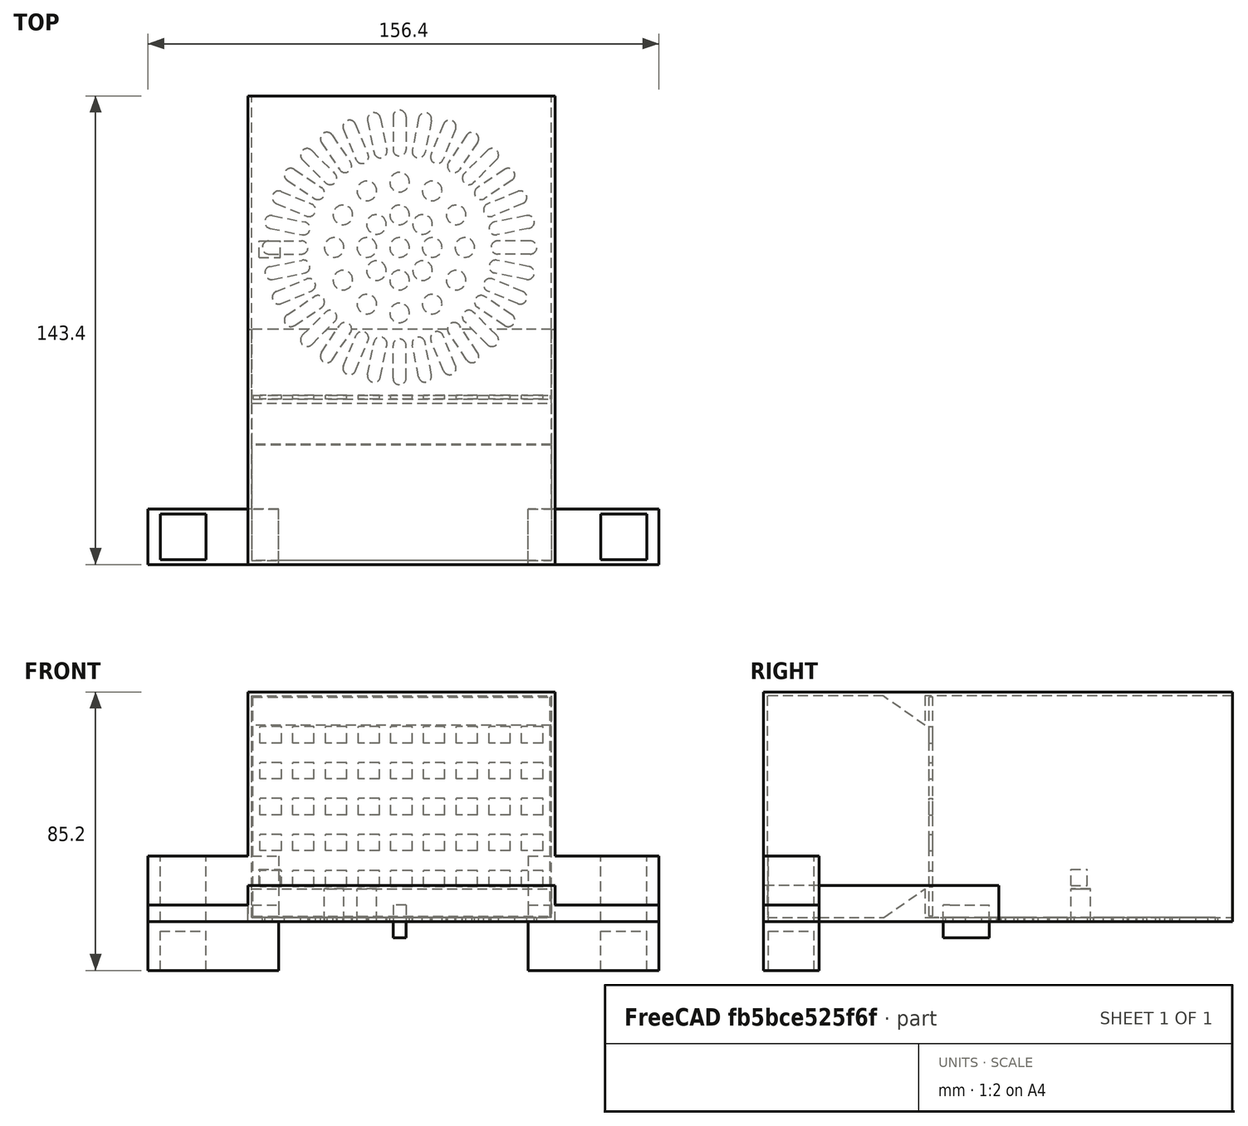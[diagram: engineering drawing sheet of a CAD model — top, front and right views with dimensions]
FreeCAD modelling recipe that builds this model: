
FCSTD DOCUMENT  (FreeCAD 0.19R24276 (Git))
Label: venti_to_aac
License: All rights reserved
LicenseURL: http://en.wikipedia.org/wiki/All_rights_reserved
objects: Part::Box×14, Part::Cut×11, Part::MultiFuse×7, Part::Cylinder×6, Part::FeaturePython×4, PartDesign::ShapeBinder×3, Sketcher::SketchObject×3, PartDesign::Pad×3, PartDesign::Body×3, Mesh::Feature×3, Part::Feature×1
note: 54 computed .brp shape members not serialized (recipe doc carries the construction recipe); baked Part::Feature solids carry a one-line shape summary decoded from their .brp

FEATURE [Part::Cylinder] Cylinder
  Angle = 360
  AttacherType = Attacher::AttachEngine3D
  Height = 1.2
  Radius = 45
FEATURE [Part::Cylinder] Cylinder002
  Angle = 360
  AttacherType = Attacher::AttachEngine3D
  Height = 10
  Radius = 3
FEATURE [Part::Cut] Cut
  Base = -> Cylinder
  Tool = -> Cylinder002
FEATURE [PartDesign::ShapeBinder] CopyCut
  TraceSupport = false
FEATURE [Sketcher::SketchObject] Sketch
  FullyConstrained = true
  MapMode = 5
  Placement = pos=(0,0,0) rot=(1,0,0;3.14159rad)
  Support = -> [CopyCut]
  sketch-geometry (4):
    g0: ArcOfCircle CenterX=-40 CenterY=0 CenterZ=0 NormalX=0 NormalY=0 NormalZ=1 AngleXU=0 Radius=2 StartAngle=1.5708 EndAngle=4.71239
    g1: ArcOfCircle CenterX=-30 CenterY=0 CenterZ=0 NormalX=0 NormalY=0 NormalZ=1 AngleXU=0 Radius=2 StartAngle=4.71239 EndAngle=7.85398
    g2: LineSegment StartX=-40 StartY=-2 StartZ=0 EndX=-30 EndY=-2 EndZ=0
    g3: LineSegment StartX=-40 StartY=2 StartZ=0 EndX=-30 EndY=2 EndZ=0
  constraints (10):
    c: Tangent(g0,g3) = 1.5708
    c: Tangent(g0,g2) = -1.5708
    c: Tangent(g2,g1) = -1.5708
    c: Tangent(g3,g1) = 1.5708
    c: Horizontal(g2)
    c: Equal(g0,g1)
    c: PointOnObject(g0,g-1)
    c: DistanceY(g0,g0) = 4
    c: DistanceX(g0,g1) = 10
    c: DistanceX(g0,g-1) = 40
FEATURE [PartDesign::Pad] Pad
  Direction = (1,1,1)
  Length = 10
  Length2 = 100
  Midplane = true
  Profile = -> Sketch
  Type = 0
FEATURE [PartDesign::Body] Body
  Group = -> [CopyCut,Sketch,Pad]
  Origin = -> Origin
  Placement = pos=(0,0,0) rot=(0,0,1;1.5708rad)
  Tip = -> Pad
FEATURE [Part::FeaturePython] Array  # Draft array (typed FeaturePython)
  Angle = 360
  ArrayType = 1
  Axis = (0,0,1)
  Base = -> Body
  Center = (0,0,0)
  Count = 32
  ExpandArray = false
  Fuse = false
  IntervalAxis = (0,0,0)
  IntervalX = (50,0,0)
  IntervalY = (0,50,0)
  IntervalZ = (0,0,50)
  NumberCircles = 3
  NumberPolar = 32
  NumberX = 2
  NumberY = 2
  NumberZ = 1
  PlacementList = 32 placements: [(0,0,0),(0,0,0),(0,0,0),(0,0,0),(0,0,0),(0,0,0),(0,0,0),(0,0,0),(0,0,0),(0,0,0),(0,0,0),(0,0,0),(0,0,0),(0,0,0),(0,0,0),(0,0,0),(0,0,0),(0,0,0),(0,0,0),(0,0,0),(0,0,0),(0,0,0),(0,0,0),(0,0,0),(0,0,0),(0,0,0),(0,0,0),(0,0,0),(0,0,0),(0,0,0),(0,0,0),(0,0,0)]
  RadialDistance = 50
  ScaleList = (32) [(1,1,1),(1,1,1),(1,1,1),(1,1,1),(1,1,1),(1,1,1),(1,1,1),(1,1,1),(1,1,1),(1,1,1),(1,1,1),(1,1,1),(1,1,1),(1,1,1),(1,1,1),(1,1,1),(1,1,1),(1,1,1),+14 more]
  Symmetry = 1
  TangentialDistance = 25
FEATURE [Part::Cut] Cut001
  Base = -> Cut
  Tool = -> Array
FEATURE [Part::Cylinder] Cylinder006
  Angle = 360
  AttacherType = Attacher::AttachEngine3D
  Height = 10
  Radius = 45
FEATURE [Part::Box] Box  label="Cube"
  AttacherType = Attacher::AttachEngine3D
  Height = 1.2
  Length = 92.8
  Placement = pos=(-46.4,-46.4,0) rot=(0,0,1;0rad)
  Width = 92.8
FEATURE [Part::Cut] Cut002
  Base = -> Box
  Tool = -> Cylinder006
FEATURE [Part::MultiFuse] Fusion
  Shapes = -> [Cut001,Cut002]
FEATURE [Part::Box] Box001  label="Cube001"
  AttacherType = Attacher::AttachEngine3D
  Height = 1.2
  Length = 92.8
  Placement = pos=(-46.4,-97,0) rot=(0,0,1;0rad)
  Width = 50.6
FEATURE [Part::MultiFuse] Fusion001
  Shapes = -> [Fusion,Box001]
FEATURE [Part::Box] Box002  label="Cube002"
  AttacherType = Attacher::AttachEngine3D
  Height = 70.2
  Length = 1.2
  Placement = pos=(46.4,-97,0) rot=(0,0,1;0rad)
  Width = 143.4
FEATURE [Part::Box] Box003  label="Cube003"
  AttacherType = Attacher::AttachEngine3D
  Height = 70.2
  Length = 1.2
  Placement = pos=(-46.4,-97,0) rot=(0,0,1;0rad)
  Width = 143.4
FEATURE [Part::Box] Box004  label="Cube004"
  AttacherType = Attacher::AttachEngine3D
  Height = 1.2
  Length = 94
  Placement = pos=(-46.4,-97,69) rot=(0,0,1;0rad)
  Width = 143.4
FEATURE [Part::MultiFuse] Fusion002
  Shapes = -> [Fusion001,Box002,Box003,Box004]
FEATURE [Part::Box] Box005  label="Cube005"
  AttacherType = Attacher::AttachEngine3D
  Height = 70.2
  Length = 94
  Placement = pos=(-46.4,-97,0) rot=(0,0,1;0rad)
  Width = 1.2
FEATURE [PartDesign::ShapeBinder] CopyFusion002001
  TraceSupport = false
FEATURE [Sketcher::SketchObject] Sketch001
  FullyConstrained = true
  MapMode = 5
  Placement = pos=(47.6,0,0) rot=(0.57735,0.57735,0.57735;2.0944rad)
  Support = -> [CopyFusion002001]
  sketch-geometry (3):
    g0: LineSegment StartX=0 StartY=0 StartZ=0 EndX=0 EndY=10 EndZ=0
    g1: LineSegment StartX=0 StartY=10 StartZ=0 EndX=-14.2815 EndY=0 EndZ=0
    g2: LineSegment StartX=-14.2815 StartY=0 StartZ=0 EndX=0 EndY=0 EndZ=0
  constraints (8):
    c: Coincident(g-1,g0)
    c: PointOnObject(g0,g-2)
    c: Coincident(g0,g1)
    c: PointOnObject(g1,g-1)
    c: Coincident(g1,g2)
    c: Coincident(g2,g0)
    c: Angle(g2,g1) = 0.610865
    c: DistanceY(g0,g0) = 10
FEATURE [PartDesign::Pad] Pad001
  Direction = (1,1,1)
  Length = 94
  Length2 = 100
  Profile = -> Sketch001
  Type = 0
FEATURE [PartDesign::Body] Body001
  Group = -> [CopyFusion002001,Sketch001,Pad001]
  Origin = -> Origin001
  Placement = pos=(-94,-47.6,0) rot=(0,0,1;0rad)
  Tip = -> Pad001
FEATURE [PartDesign::ShapeBinder] CopyFusion002002
  TraceSupport = false
FEATURE [Sketcher::SketchObject] Sketch002
  FullyConstrained = true
  MapMode = 5
  Placement = pos=(47.6,0,0) rot=(0.57735,0.57735,0.57735;2.0944rad)
  Support = -> [CopyFusion002002]
  sketch-geometry (3):
    g0: LineSegment StartX=0 StartY=0 StartZ=0 EndX=0 EndY=10 EndZ=0
    g1: LineSegment StartX=0 StartY=10 StartZ=0 EndX=-14.2815 EndY=0 EndZ=0
    g2: LineSegment StartX=-14.2815 StartY=0 StartZ=0 EndX=0 EndY=0 EndZ=0
  constraints (8):
    c: Coincident(g-1,g0)
    c: PointOnObject(g0,g-2)
    c: Coincident(g0,g1)
    c: PointOnObject(g1,g-1)
    c: Coincident(g1,g2)
    c: Coincident(g2,g0)
    c: Angle(g2,g1) = 0.610865
    c: DistanceY(g0,g0) = 10
FEATURE [PartDesign::Pad] Pad002
  Direction = (1,1,1)
  Length = 94
  Length2 = 100
  Profile = -> Sketch002
  Type = 0
FEATURE [PartDesign::Body] Body002
  Group = -> [CopyFusion002002,Sketch002,Pad002]
  Origin = -> Origin002
  Placement = pos=(95.2,-47.6,70) rot=(0,1,0;3.14159rad)
  Tip = -> Pad002
FEATURE [Part::MultiFuse] Fusion003
  Shapes = -> [Fusion002,Box005]
FEATURE [Part::MultiFuse] Fusion004  label="caja_grande"
  Shapes = -> [Fusion003,Body002,Body001]
FEATURE [Part::Box] Box006  label="Cube006"
  AttacherType = Attacher::AttachEngine3D
  Height = 1.2
  Length = 91
  Placement = pos=(-44.9,0,1.6) rot=(1,0,0;1.5708rad)
  Width = 67
FEATURE [Part::Box] Box007  label="Cube007"
  AttacherType = Attacher::AttachEngine3D
  Height = 5
  Length = 6.5
  Placement = pos=(-43,-3,11) rot=(0,0,1;0rad)
  Width = 5
FEATURE [Part::FeaturePython] Array001  # Draft array (typed FeaturePython)
  Angle = 360
  ArrayType = 0
  Axis = (0,0,1)
  Base = -> Box007
  Center = (0,0,0)
  Count = 45
  ExpandArray = false
  Fuse = false
  IntervalAxis = (0,0,0)
  IntervalX = (10,0,0)
  IntervalY = (0,10,0)
  IntervalZ = (0,0,11)
  NumberCircles = 3
  NumberPolar = 5
  NumberX = 9
  NumberY = 1
  NumberZ = 5
  Placement = pos=(0.35,0,-0.4) rot=(0,0,1;0rad)
  PlacementList = 45 placements: [(-43,-3,11),(-43,-3,22),(-43,-3,33),(-43,-3,44),(-43,-3,55),(-33,-3,11),(-33,-3,22),(-33,-3,33),(-33,-3,44),(-33,-3,55),(-23,-3,11),(-23,-3,22),(-23,-3,33),(-23,-3,44),(-23,-3,55),(-13,-3,11),(-13,-3,22),(-13,-3,33),(-13,-3,44),(-13,-3,55),(-3,-3,11),(-3,-3,22),(-3,-3,33),(-3,-3,44),(-3,-3,55),(7,-3,11),(7,-3,22),(7,-3,33),(7,-3,44),(7,-3,55),(17,-3,11),(17,-3,22),(17,-3,33),(17,-3,44),(17,-3,55),+10 more]
  RadialDistance = 50
  ScaleList = (45) [(1,1,1),(1,1,1),(1,1,1),(1,1,1),(1,1,1),(1,1,1),(1,1,1),(1,1,1),(1,1,1),(1,1,1),(1,1,1),(1,1,1),(1,1,1),(1,1,1),(1,1,1),(1,1,1),(1,1,1),(1,1,1),+27 more]
  Symmetry = 1
  TangentialDistance = 25
FEATURE [Part::Cut] Cut003  label="rejilla"
  Base = -> Box006
  Placement = pos=(0,-45.2,0) rot=(0,0,1;0rad)
  Tool = -> Array001
FEATURE [Part::Box] Box008  label="Cube008"
  AttacherType = Attacher::AttachEngine3D
  Height = 20
  Length = 40
  Placement = pos=(-77,-97,-15) rot=(0,0,1;0rad)
  Width = 17
FEATURE [Part::Box] Box009  label="Cube009"
  AttacherType = Attacher::AttachEngine3D
  Height = 20
  Length = 40
  Placement = pos=(39.4,-97,-15) rot=(0,0,1;0rad)
  Width = 17
FEATURE [Part::Box] Box010  label="Cube010"
  AttacherType = Attacher::AttachEngine3D
  Height = 52
  Length = 14
  Placement = pos=(61.6,-95.5,-15) rot=(0,0,1;0rad)
  Width = 14
FEATURE [Part::Box] Box011  label="Cube011"
  AttacherType = Attacher::AttachEngine3D
  Height = 35
  Length = 14
  Placement = pos=(-73.2,-95.5,-15) rot=(0,0,1;0rad)
  Width = 14
FEATURE [Part::Cut] Cut004  label="pata1"
  Base = -> Box008
  Placement = pos=(0,0,15) rot=(0,0,1;0rad)
  Tool = -> Box011
FEATURE [Part::Cut] Cut005  label="pata2"
  Base = -> Box009
  Placement = pos=(0,0,15) rot=(0,0,1;0rad)
  Tool = -> Box010
FEATURE [Part::Box] Box012  label="Cube012"
  AttacherType = Attacher::AttachEngine3D
  Height = 80
  Length = 160
  Placement = pos=(-80,-25,-5) rot=(0,0,1;0rad)
  Width = 83
FEATURE [Part::MultiFuse] Fusion005002  label="acc"
  Shapes = -> [Fusion004,Cut004,Cut005]
FEATURE [Part::Feature] Fusion005002001  label="acc001"
  shape: bbox 156.4 x 143.4 x 85.2 mm, 228 faces (baked)
FEATURE [Part::Cut] Cut006
  Base = -> Fusion005002001
  Tool = -> Box012
FEATURE [Part::Box] Box013  label="Cube013"
  AttacherType = Attacher::AttachEngine3D
  Height = 74
  Length = 160
  Placement = pos=(-80,-103,11) rot=(0,0,1;0rad)
  Width = 93
FEATURE [Part::Cut] Cut007  label="test"
  Base = -> Cut006
  Tool = -> Box013
FEATURE [Mesh::Feature] Mesh  label="test (Meshed)"
FEATURE [Part::Cylinder] Cylinder007
  Angle = 360
  AttacherType = Attacher::AttachEngine3D
  Height = 10
  Placement = pos=(-10,0,0) rot=(0,0,1;0rad)
  Radius = 3
FEATURE [Part::Cylinder] Cylinder008
  Angle = 360
  AttacherType = Attacher::AttachEngine3D
  Height = 10
  Placement = pos=(-20,0,0) rot=(0,0,1;0rad)
  Radius = 3
FEATURE [Part::FeaturePython] Array002  # Draft array (typed FeaturePython)
  Angle = 360
  ArrayType = 1
  Axis = (0,0,1)
  Base = -> Cylinder007
  Center = (0,0,0)
  Count = 8
  ExpandArray = false
  Fuse = false
  IntervalAxis = (0,0,0)
  IntervalX = (50,0,0)
  IntervalY = (0,50,0)
  IntervalZ = (0,0,50)
  NumberCircles = 3
  NumberPolar = 8
  NumberX = 2
  NumberY = 2
  NumberZ = 1
  PlacementList = 8 placements: [(-10,0,0),(-7.07107,-7.07107,0),(0,-10,0),(7.07107,-7.07107,0),(10,-1.22465e-15,0),(7.07107,7.07107,0),(1.77636e-15,10,0),(-7.07107,7.07107,0)]
  RadialDistance = 50
  ScaleList = (8) [(1,1,1),(1,1,1),(1,1,1),(1,1,1),(1,1,1),(1,1,1),(1,1,1),(1,1,1)]
  Symmetry = 1
  TangentialDistance = 25
FEATURE [Part::FeaturePython] Array003  # Draft array (typed FeaturePython)
  Angle = 360
  ArrayType = 1
  Axis = (0,0,1)
  Base = -> Cylinder008
  Center = (0,0,0)
  Count = 12
  ExpandArray = false
  Fuse = false
  IntervalAxis = (0,0,0)
  IntervalX = (50,0,0)
  IntervalY = (0,50,0)
  IntervalZ = (0,0,50)
  NumberCircles = 3
  NumberPolar = 12
  NumberX = 2
  NumberY = 2
  NumberZ = 1
  PlacementList = 12 placements: [(-20,0,0),(-17.3205,-10,0),(-10,-17.3205,0),(0,-20,0),(10,-17.3205,0),(17.3205,-10,0),(20,-2.44929e-15,0),(17.3205,10,0),(10,17.3205,0),(3.55271e-15,20,0),(-10,17.3205,0),(-17.3205,10,0)]
  RadialDistance = 50
  ScaleList = (12) [(1,1,1),(1,1,1),(1,1,1),(1,1,1),(1,1,1),(1,1,1),(1,1,1),(1,1,1),(1,1,1),(1,1,1),(1,1,1),(1,1,1)]
  Symmetry = 1
  TangentialDistance = 25
FEATURE [Part::Cut] Cut008
  Base = -> Cut001
  Refine = true
  Tool = -> Array002
FEATURE [Part::Cut] Cut009  label="nuevo panel"
  Base = -> Cut008
  Refine = true
  Tool = -> Array003
FEATURE [Part::Cylinder] Cylinder009
  Angle = 360
  AttacherType = Attacher::AttachEngine3D
  Height = 1.2
  Radius = 45
FEATURE [Part::Cut] Cut010
  Base = -> Fusion005002
  Refine = true
  Tool = -> Cylinder009
FEATURE [Part::MultiFuse] Fusion005002002  label="aircc2"
  Refine = true
  Shapes = -> [Cut009,Cut010]
FEATURE [Mesh::Feature] Mesh001  label="aircc2 (Meshed)"
FEATURE [Mesh::Feature] Mesh002  label="rejilla (Meshed)"
